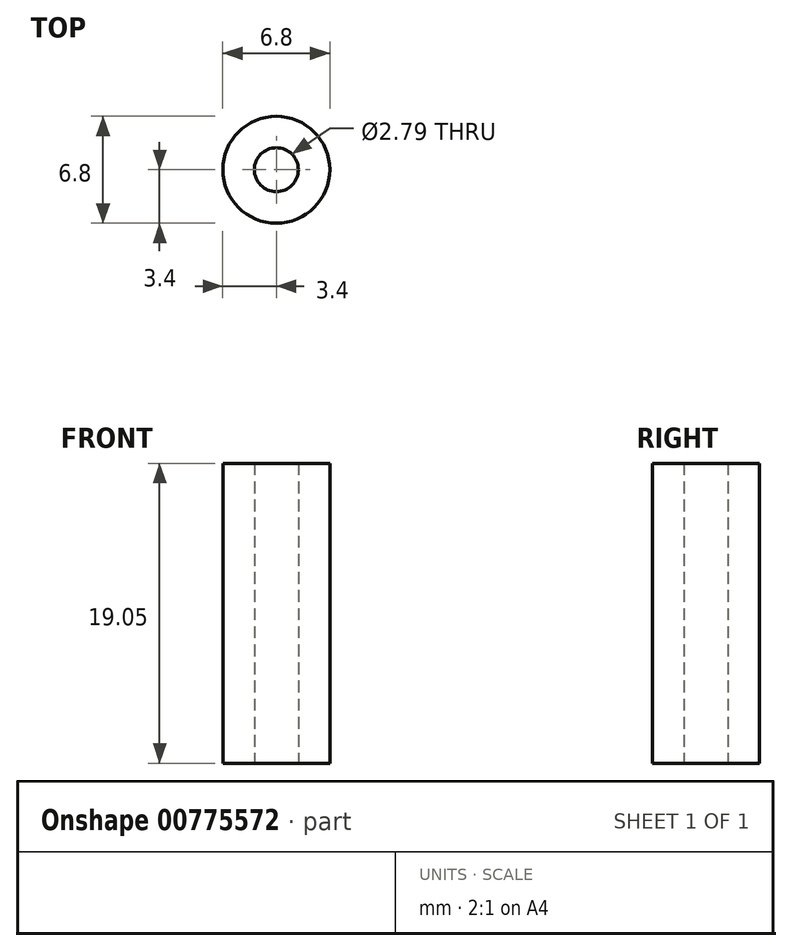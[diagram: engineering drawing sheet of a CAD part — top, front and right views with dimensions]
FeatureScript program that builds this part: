
annotation { "Feature Type Name" : "Feature", "Feature Type Description" : "" }
export const myFeature = defineFeature(function(context is Context, id is Id, definition is map)
    precondition{}
    {
        {
            var Q0;
            Q0=qCreatedBy(makeId("Top.planeOp"),FACE);
            var sketch = newSketch(context, id + "F0", { "sketchPlane" : qUnion([Q0])});
            skCircle(sketch, "E0", {"center": v(0, 0) * mm, "radius": 1.4 * mm});
            skCircle(sketch, "E1", {"center": v(0, 0) * mm, "radius": 3.4 * mm});
            skSolve(sketch);
        }
        {
            var Q0;
            Q0 = qSketchRegion(id + "F0", true);
            extrude(context, id + "F1", {"entities" : qUnion([Q0]), "depth" : 19.05 * mm, "offsetDistance" : 25.4 * mm});
        }
    });
